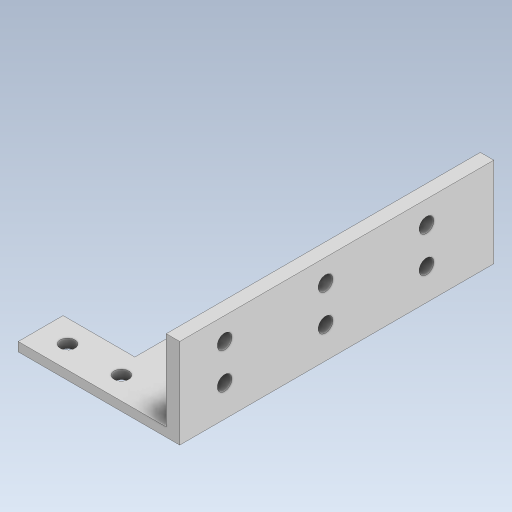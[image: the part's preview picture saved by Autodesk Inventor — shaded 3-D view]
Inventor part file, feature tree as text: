
AUTODESK INVENTOR PART (.ipt)
format: ipt  version: 2023.5 (Build 275446000, 446)  size: 147,456 bytes
history: native  units: mm
features: extrude x3, sketch x2
ambient origin geometry x8: Origin, YZ Plane, XZ Plane, XY Plane, X Axis, Y Axis, Z Axis, Center Point
bodies: Solid1 (feature_tree)
feature tree (5):
  sketch  "Sketch1"  dims[d0=3.3mm d1=3.3mm]
  extrude  "Extrusion1"  Depth=3.3mm
  extrude  "Extrusion2"  Depth=20.0mm
  extrude  "Extrusion3"  Depth=20.0mm
  sketch  "Sketch2"  dims[d2=12.0mm d3=3.3mm d4=12.5mm d5=20.0mm d6=3.3mm d7=40.0mm d8=20.0mm d9=35.0mm d10=2.0mm d11=0.0mm d12=20.0mm d13=0.0mm d14=3.3mm d15=10.0mm d16=3.3mm d18=3.3mm d19=20.0mm d20=0.0mm d21=5.0mm d22=5.0mm d23=5.0mm d24=15.0mm d25=3.3mm d26=20.0mm d27=3.3mm d28=40.0mm]
